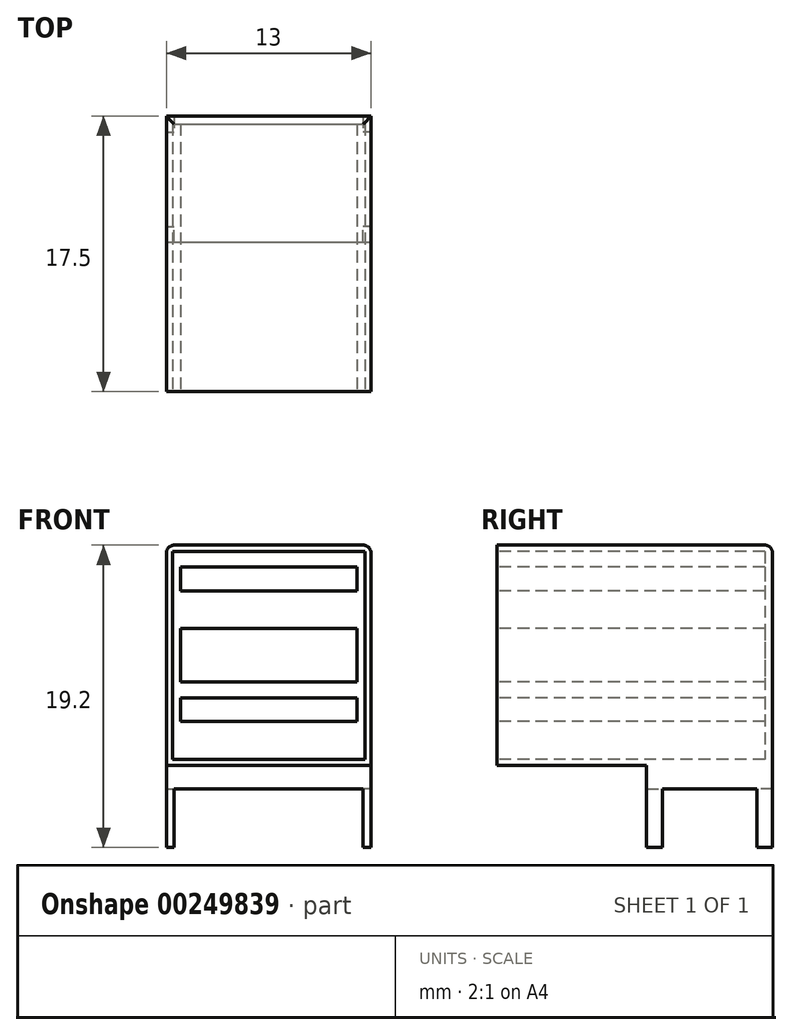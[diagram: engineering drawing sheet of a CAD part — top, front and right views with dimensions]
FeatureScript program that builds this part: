
annotation { "Feature Type Name" : "Feature", "Feature Type Description" : "" }
export const myFeature = defineFeature(function(context is Context, id is Id, definition is map)
    precondition{}
    {
        {
            var Q0;
            Q0=qCreatedBy(makeId("Front.planeOp"),FACE);
            var sketch = newSketch(context, id + "F0", { "sketchPlane" : qUnion([Q0])});
            skLineSegment(sketch, "E0.bottom", {"start": v(0, 0) * mm, "end": v(13, 0) * mm});
            skLineSegment(sketch, "E0.top", {"start": v(0, 14) * mm, "end": v(13, 14) * mm});
            skLineSegment(sketch, "E0.left", {"start": v(0, 0) * mm, "end": v(0, 14) * mm});
            skLineSegment(sketch, "E0.right", {"start": v(13, 0) * mm, "end": v(13, 14) * mm});
            skSolve(sketch);
        }
        {
            var Q0;
            Q0 = qSketchRegion(id + "F0", true);
            extrude(context, id + "F1", {"entities" : qUnion([Q0]), "depth" : 17.5 * mm});
        }
        {
            var Q0;
            Q0=makeQuery(id+"F1.opExtrude","CAP_FACE",FACE,{"disambiguationData":[OSD([sQuery(id+"F0.wireOp",EDGE,"E0.bottom"),sQuery(id+"F0.wireOp",EDGE,"E0.top"),sQuery(id+"F0.wireOp",EDGE,"E0.left"),sQuery(id+"F0.wireOp",EDGE,"E0.right")])],"isStart":false});
            var sketch = newSketch(context, id + "F2", { "sketchPlane" : qUnion([Q0])});
            skLineSegment(sketch, "E1.bottom", {"start": v(0.4, 13.6) * mm, "end": v(12.6, 13.6) * mm});
            skLineSegment(sketch, "E1.top", {"start": v(0.4, 0.4) * mm, "end": v(12.6, 0.4) * mm});
            skLineSegment(sketch, "E1.left", {"start": v(0.4, 13.6) * mm, "end": v(0.4, 0.4) * mm});
            skLineSegment(sketch, "E1.right", {"start": v(12.6, 13.6) * mm, "end": v(12.6, 0.4) * mm});
            skLineSegment(sketch, "E2", {"start": v(6.5, 13.6) * mm, "end": v(6.5, 0.4) * mm, "construction": true});
            skLineSegment(sketch, "E3", {"start": v(0.4, 7) * mm, "end": v(12.6, 7) * mm, "construction": true});
            skLineSegment(sketch, "E4.bottom", {"start": v(0.9, 8.7) * mm, "end": v(12.1, 8.7) * mm});
            skLineSegment(sketch, "E4.top", {"start": v(0.9, 5.3) * mm, "end": v(12.1, 5.3) * mm});
            skLineSegment(sketch, "E4.left", {"start": v(0.9, 8.7) * mm, "end": v(0.9, 5.3) * mm});
            skLineSegment(sketch, "E4.right", {"start": v(12.1, 8.7) * mm, "end": v(12.1, 5.3) * mm});
            skLineSegment(sketch, "E5.bottom", {"start": v(0.9, 12.6) * mm, "end": v(12.1, 12.6) * mm});
            skLineSegment(sketch, "E5.top", {"start": v(0.9, 11.1) * mm, "end": v(12.1, 11.1) * mm});
            skLineSegment(sketch, "E5.left", {"start": v(0.9, 12.6) * mm, "end": v(0.9, 11.1) * mm});
            skLineSegment(sketch, "E5.right", {"start": v(12.1, 12.6) * mm, "end": v(12.1, 11.1) * mm});
            skLineSegment(sketch, "E6.bottom", {"start": v(0.9, 4.3) * mm, "end": v(12.1, 4.3) * mm});
            skLineSegment(sketch, "E6.top", {"start": v(0.9, 2.8) * mm, "end": v(12.1, 2.8) * mm});
            skLineSegment(sketch, "E6.left", {"start": v(0.9, 4.3) * mm, "end": v(0.9, 2.8) * mm});
            skLineSegment(sketch, "E6.right", {"start": v(12.1, 4.3) * mm, "end": v(12.1, 2.8) * mm});
            skSolve(sketch);
        }
        {
            var Q0;
            Q0 = qSketchRegion(id + "F2", true);
            extrude(context, id + "F3", {"entities" : qUnion([Q0]), "operationType" : NewBodyOperationType.REMOVE, "oppositeDirection" : true, "depth" : 17 * mm});
        }
        {
            var Q0;
            Q0=makeQuery(id+"F1.opExtrude","SWEPT_FACE",FACE,{"disambiguationData":[OSD([sQuery(id+"F0.wireOp",EDGE,"E0.bottom")])]});
            var sketch = newSketch(context, id + "F4", { "sketchPlane" : qUnion([Q0])});
            skLineSegment(sketch, "E7.bottom", {"start": v(0, 0) * mm, "end": v(13, 0) * mm});
            skLineSegment(sketch, "E7.top", {"start": v(0, 8) * mm, "end": v(13, 8) * mm});
            skLineSegment(sketch, "E7.left", {"start": v(0, 0) * mm, "end": v(0, 8) * mm});
            skLineSegment(sketch, "E7.right", {"start": v(13, 0) * mm, "end": v(13, 8) * mm});
            skSolve(sketch);
        }
        {
            var Q0;
            Q0 = qSketchRegion(id + "F4", true);
            extrude(context, id + "F5", {"entities" : qUnion([Q0]), "operationType" : NewBodyOperationType.ADD, "depth" : 1.5 * mm});
        }
        {
            var Q0;
            Q0=makeQuery(id+"F5.opExtrude","CAP_FACE",FACE,{"disambiguationData":[OSD([sQuery(id+"F4.wireOp",EDGE,"E7.bottom"),sQuery(id+"F4.wireOp",EDGE,"E7.top"),sQuery(id+"F4.wireOp",EDGE,"E7.left"),sQuery(id+"F4.wireOp",EDGE,"E7.right")])],"isStart":false});
            var sketch = newSketch(context, id + "F6", { "sketchPlane" : qUnion([Q0])});
            skLineSegment(sketch, "E8.bottom", {"start": v(0, 8) * mm, "end": v(0.5, 8) * mm});
            skLineSegment(sketch, "E8.top", {"start": v(0, 7) * mm, "end": v(0.5, 7) * mm});
            skLineSegment(sketch, "E8.left", {"start": v(0, 8) * mm, "end": v(0, 7) * mm});
            skLineSegment(sketch, "E8.right", {"start": v(0.5, 8) * mm, "end": v(0.5, 7) * mm});
            skLineSegment(sketch, "E9.bottom", {"start": v(0, 0) * mm, "end": v(0.5, 0) * mm});
            skLineSegment(sketch, "E9.top", {"start": v(0, 1) * mm, "end": v(0.5, 1) * mm});
            skLineSegment(sketch, "E9.left", {"start": v(0, 0) * mm, "end": v(0, 1) * mm});
            skLineSegment(sketch, "E9.right", {"start": v(0.5, 0) * mm, "end": v(0.5, 1) * mm});
            skLineSegment(sketch, "E10.bottom", {"start": v(13, 8) * mm, "end": v(12.5, 8) * mm});
            skLineSegment(sketch, "E10.top", {"start": v(13, 7) * mm, "end": v(12.5, 7) * mm});
            skLineSegment(sketch, "E10.left", {"start": v(13, 8) * mm, "end": v(13, 7) * mm});
            skLineSegment(sketch, "E10.right", {"start": v(12.5, 8) * mm, "end": v(12.5, 7) * mm});
            skLineSegment(sketch, "E11.bottom", {"start": v(13, 0) * mm, "end": v(12.5, 0) * mm});
            skLineSegment(sketch, "E11.top", {"start": v(13, 1) * mm, "end": v(12.5, 1) * mm});
            skLineSegment(sketch, "E11.left", {"start": v(13, 0) * mm, "end": v(13, 1) * mm});
            skLineSegment(sketch, "E11.right", {"start": v(12.5, 0) * mm, "end": v(12.5, 1) * mm});
            skSolve(sketch);
        }
        {
            var Q0;
            Q0 = qSketchRegion(id + "F6", true);
            extrude(context, id + "F7", {"entities" : qUnion([Q0]), "operationType" : NewBodyOperationType.ADD, "depth" : 3.7 * mm});
        }
        {
            var Q0;
            Q0=makeQuery(id+"F1.opExtrude","SWEPT_EDGE",EDGE,{"disambiguationData":[OSD([sQuery(id+"F0.wireOp",EDGE,"E0.top"),sQuery(id+"F0.wireOp",EDGE,"E0.right")])]});
            var Q1;
            Q1=makeQuery(id+"F1.opExtrude","CAP_EDGE",EDGE,{"disambiguationData":[OSD([sQuery(id+"F0.wireOp",EDGE,"E0.top")])],"isStart":true});
            var Q2;
            Q2=makeQuery(id+"F1.opExtrude","SWEPT_EDGE",EDGE,{"disambiguationData":[OSD([sQuery(id+"F0.wireOp",EDGE,"E0.top"),sQuery(id+"F0.wireOp",EDGE,"E0.left")])]});
            fillet(context, id + "F8", {"entities" : qUnion([Q0, Q1, Q2]), "radius" : 0.5 * mm, "tangentPropagation" : true, "allowEdgeOverflow" : false});
        }
    });
